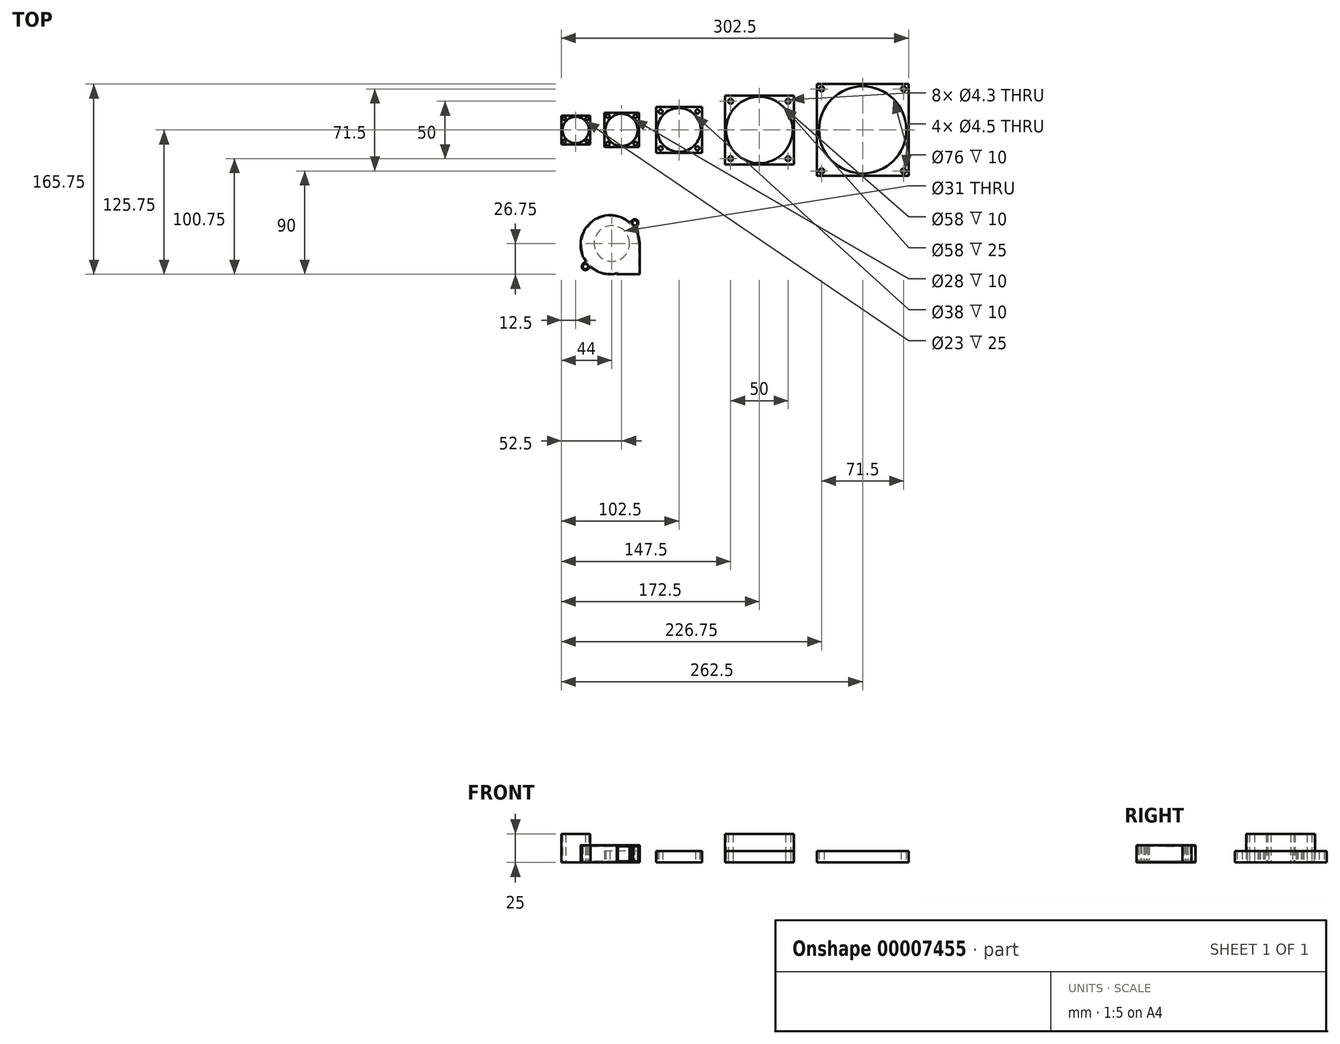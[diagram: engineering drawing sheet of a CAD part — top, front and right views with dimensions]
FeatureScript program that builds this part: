
annotation { "Feature Type Name" : "Feature", "Feature Type Description" : "" }
export const myFeature = defineFeature(function(context is Context, id is Id, definition is map)
    precondition{}
    {
        {
            var Q0;
            Q0=qCreatedBy(makeId("Top.planeOp"),FACE);
            var sketch = newSketch(context, id + "F0", { "sketchPlane" : qUnion([Q0])});
            skLineSegment(sketch, "E0", {"start": v(0, 0) * mm, "end": v(333.95, 0) * mm, "construction": true});
            skLineSegment(sketch, "E1.rect.bottom", {"start": v(32.5, 12.5) * mm, "end": v(7.5, 12.5) * mm});
            skLineSegment(sketch, "E1.rect.top", {"start": v(32.5, -12.5) * mm, "end": v(7.5, -12.5) * mm});
            skLineSegment(sketch, "E1.rect.left", {"start": v(32.5, 12.5) * mm, "end": v(32.5, -12.5) * mm});
            skLineSegment(sketch, "E1.rect.right", {"start": v(7.5, 12.5) * mm, "end": v(7.5, -12.5) * mm});
            skPoint(sketch, "E1.rect.middle", {"position": v(20, 0) * mm});
            skLineSegment(sketch, "E2.rect.bottom", {"start": v(30, 10) * mm, "end": v(10, 10) * mm, "construction": true});
            skLineSegment(sketch, "E2.rect.top", {"start": v(30, -10) * mm, "end": v(10, -10) * mm, "construction": true});
            skLineSegment(sketch, "E2.rect.left", {"start": v(30, 10) * mm, "end": v(30, -10) * mm, "construction": true});
            skLineSegment(sketch, "E2.rect.right", {"start": v(10, 10) * mm, "end": v(10, -10) * mm, "construction": true});
            skLineSegment(sketch, "E3.rect.bottom", {"start": v(72, 12) * mm, "end": v(48, 12) * mm, "construction": true});
            skLineSegment(sketch, "E3.rect.top", {"start": v(72, -12) * mm, "end": v(48, -12) * mm, "construction": true});
            skLineSegment(sketch, "E3.rect.left", {"start": v(72, 12) * mm, "end": v(72, -12) * mm, "construction": true});
            skLineSegment(sketch, "E3.rect.right", {"start": v(48, 12) * mm, "end": v(48, -12) * mm, "construction": true});
            skPoint(sketch, "E3.rect.middle", {"position": v(60, 0) * mm});
            skLineSegment(sketch, "E4.rect.bottom", {"start": v(126, 16) * mm, "end": v(94, 16) * mm, "construction": true});
            skLineSegment(sketch, "E4.rect.top", {"start": v(126, -16) * mm, "end": v(94, -16) * mm, "construction": true});
            skLineSegment(sketch, "E4.rect.left", {"start": v(126, 16) * mm, "end": v(126, -16) * mm, "construction": true});
            skLineSegment(sketch, "E4.rect.right", {"start": v(94, 16) * mm, "end": v(94, -16) * mm, "construction": true});
            skPoint(sketch, "E4.rect.middle", {"position": v(110, 0) * mm});
            skLineSegment(sketch, "E5.rect.bottom", {"start": v(305.75, 35.75) * mm, "end": v(234.25, 35.75) * mm, "construction": true});
            skLineSegment(sketch, "E5.rect.top", {"start": v(305.75, -35.75) * mm, "end": v(234.25, -35.75) * mm, "construction": true});
            skLineSegment(sketch, "E5.rect.left", {"start": v(305.75, 35.75) * mm, "end": v(305.75, -35.75) * mm, "construction": true});
            skLineSegment(sketch, "E5.rect.right", {"start": v(234.25, 35.75) * mm, "end": v(234.25, -35.75) * mm, "construction": true});
            skPoint(sketch, "E5.rect.middle", {"position": v(270, 0) * mm});
            skLineSegment(sketch, "E6.rect.bottom", {"start": v(75, 15) * mm, "end": v(45, 15) * mm});
            skLineSegment(sketch, "E6.rect.top", {"start": v(75, -15) * mm, "end": v(45, -15) * mm});
            skLineSegment(sketch, "E6.rect.left", {"start": v(75, 15) * mm, "end": v(75, -15) * mm});
            skLineSegment(sketch, "E6.rect.right", {"start": v(45, 15) * mm, "end": v(45, -15) * mm});
            skLineSegment(sketch, "E7.rect.bottom", {"start": v(90, 20) * mm, "end": v(130, 20) * mm});
            skLineSegment(sketch, "E7.rect.top", {"start": v(90, -20) * mm, "end": v(130, -20) * mm});
            skLineSegment(sketch, "E7.rect.left", {"start": v(90, 20) * mm, "end": v(90, -20) * mm});
            skLineSegment(sketch, "E7.rect.right", {"start": v(130, 20) * mm, "end": v(130, -20) * mm});
            skLineSegment(sketch, "E8.rect.bottom", {"start": v(230, 40) * mm, "end": v(310, 40) * mm});
            skLineSegment(sketch, "E8.rect.top", {"start": v(230, -40) * mm, "end": v(310, -40) * mm});
            skLineSegment(sketch, "E8.rect.left", {"start": v(230, 40) * mm, "end": v(230, -40) * mm});
            skLineSegment(sketch, "E8.rect.right", {"start": v(310, 40) * mm, "end": v(310, -40) * mm});
            skCircle(sketch, "E9", {"center": v(20, 0) * mm, "radius": 11.5 * mm});
            skCircle(sketch, "E10", {"center": v(10, 10) * mm, "radius": 1.4 * mm});
            skCircle(sketch, "E11", {"center": v(30, 10) * mm, "radius": 1.4 * mm});
            skCircle(sketch, "E12", {"center": v(30, -10) * mm, "radius": 1.4 * mm});
            skCircle(sketch, "E13", {"center": v(10, -10) * mm, "radius": 1.4 * mm});
            skCircle(sketch, "E14", {"center": v(48, 12) * mm, "radius": 1.6 * mm});
            skCircle(sketch, "E15", {"center": v(72, 12) * mm, "radius": 1.6 * mm});
            skCircle(sketch, "E16", {"center": v(72, -12) * mm, "radius": 1.6 * mm});
            skCircle(sketch, "E17", {"center": v(48, -12) * mm, "radius": 1.6 * mm});
            skCircle(sketch, "E18", {"center": v(60, 0) * mm, "radius": 14 * mm});
            skCircle(sketch, "E19", {"center": v(94, 16) * mm, "radius": 1.75 * mm});
            skCircle(sketch, "E20", {"center": v(126, 16) * mm, "radius": 1.75 * mm});
            skCircle(sketch, "E21", {"center": v(126, -16) * mm, "radius": 1.75 * mm});
            skCircle(sketch, "E22", {"center": v(94, -16) * mm, "radius": 1.75 * mm});
            skCircle(sketch, "E23", {"center": v(110, 0) * mm, "radius": 19 * mm});
            skLineSegment(sketch, "E24.rect.bottom", {"start": v(210, 30) * mm, "end": v(150, 30) * mm});
            skLineSegment(sketch, "E24.rect.top", {"start": v(210, -30) * mm, "end": v(150, -30) * mm});
            skLineSegment(sketch, "E24.rect.left", {"start": v(210, 30) * mm, "end": v(210, -30) * mm});
            skLineSegment(sketch, "E24.rect.right", {"start": v(150, 30) * mm, "end": v(150, -30) * mm});
            skPoint(sketch, "E24.rect.middle", {"position": v(180, 0) * mm});
            skLineSegment(sketch, "E25.rect.bottom", {"start": v(205, 25) * mm, "end": v(155, 25) * mm, "construction": true});
            skLineSegment(sketch, "E25.rect.top", {"start": v(205, -25) * mm, "end": v(155, -25) * mm, "construction": true});
            skLineSegment(sketch, "E25.rect.left", {"start": v(205, 25) * mm, "end": v(205, -25) * mm, "construction": true});
            skLineSegment(sketch, "E25.rect.right", {"start": v(155, 25) * mm, "end": v(155, -25) * mm, "construction": true});
            skCircle(sketch, "E26", {"center": v(155, 25) * mm, "radius": 2.15 * mm});
            skCircle(sketch, "E27", {"center": v(205, 25) * mm, "radius": 2.15 * mm});
            skCircle(sketch, "E28", {"center": v(205, -25) * mm, "radius": 2.15 * mm});
            skCircle(sketch, "E29", {"center": v(155, -25) * mm, "radius": 2.15 * mm});
            skCircle(sketch, "E30", {"center": v(180, 0) * mm, "radius": 29 * mm});
            skCircle(sketch, "E31", {"center": v(234.25, 35.75) * mm, "radius": 2.25 * mm});
            skCircle(sketch, "E32", {"center": v(305.75, 35.75) * mm, "radius": 2.25 * mm});
            skCircle(sketch, "E33", {"center": v(305.75, -35.75) * mm, "radius": 2.25 * mm});
            skCircle(sketch, "E34", {"center": v(234.25, -35.75) * mm, "radius": 2.25 * mm});
            skCircle(sketch, "E35", {"center": v(270, 0) * mm, "radius": 38 * mm});
            skPoint(sketch, "E36", {"position": v(50, -100) * mm});
            skPoint(sketch, "E37", {"position": v(28.5, -119) * mm});
            skPoint(sketch, "E38", {"position": v(71.5, -81) * mm});
            skCircle(sketch, "E39", {"center": v(71.5, -81) * mm, "radius": 2.2 * mm});
            skCircle(sketch, "E40", {"center": v(28.5, -119) * mm, "radius": 2.2 * mm});
            skArc(sketch, "E41", {"start": v(73.62, -83.4) * mm, "mid": v(73.9, -78.88) * mm, "end": v(69.38, -78.6) * mm});
            skArc(sketch, "E42", {"start": v(26.38, -116.6) * mm, "mid": v(26.1, -121.12) * mm, "end": v(30.62, -121.4) * mm});
            skLineSegment(sketch, "E43", {"start": v(50, -100) * mm, "end": v(24.25, -100) * mm, "construction": true});
            skLineSegment(sketch, "E44", {"start": v(50, -100) * mm, "end": v(50, -125.75) * mm, "construction": true});
            skLineSegment(sketch, "E45", {"start": v(50, -100) * mm, "end": v(75.75, -100) * mm, "construction": true});
            skLineSegment(sketch, "E46", {"start": v(28.5, -119) * mm, "end": v(71.5, -81) * mm, "construction": true});
            skLineSegment(sketch, "E47", {"start": v(75.75, -100) * mm, "end": v(75.75, -125.75) * mm});
            skLineSegment(sketch, "E48", {"start": v(75.75, -125.75) * mm, "end": v(55.75, -125.75) * mm});
            skLineSegment(sketch, "E49", {"start": v(55.75, -125.75) * mm, "end": v(55.75, -125.1) * mm});
            skLineSegment(sketch, "E50", {"start": v(73.62, -83.4) * mm, "end": v(30.62, -121.4) * mm});
            skLineSegment(sketch, "E51", {"start": v(26.38, -116.6) * mm, "end": v(69.38, -78.6) * mm});
            skArc(sketch, "E52.trimOffspring", {"start": v(32.97, -119.32) * mm, "mid": v(67.05, -119.3) * mm, "end": v(71.26, -85.48) * mm});
            skArc(sketch, "E53.trimOffspring", {"start": v(67.03, -80.68) * mm, "mid": v(32.95, -80.7) * mm, "end": v(28.74, -114.52) * mm});
            skCircle(sketch, "E54", {"center": v(51.5, -99) * mm, "radius": 15.5 * mm});
            skSolve(sketch);
        }
        {
            var Q0;
            Q0=makeQuery(id+"F0.imprint","IMPRINT",FACE,{"disambiguationData":[TD([[makeQuery(id+"F0.imprint","IMPRINT",EDGE,{"derivedFrom":sQuery(id+"F0.wireOp",EDGE,"E1.rect.bottom")}),1.0]])]});
            extrude(context, id + "F1", {"entities" : qUnion([Q0]), "depth" : 25 * mm});
        }
        {
            var Q0;
            Q0=makeQuery(id+"F0.imprint","IMPRINT",FACE,{"disambiguationData":[TD([[makeQuery(id+"F0.imprint","IMPRINT",EDGE,{"derivedFrom":sQuery(id+"F0.wireOp",EDGE,"E6.rect.bottom")}),1.0]])]});
            extrude(context, id + "F2", {"entities" : qUnion([Q0]), "depth" : 10 * mm});
        }
        {
            var Q0;
            Q0=makeQuery(id+"F0.imprint","IMPRINT",FACE,{"disambiguationData":[TD([[makeQuery(id+"F0.imprint","IMPRINT",EDGE,{"derivedFrom":sQuery(id+"F0.wireOp",EDGE,"E7.rect.bottom")}),-1.0]])]});
            extrude(context, id + "F3", {"entities" : qUnion([Q0]), "depth" : 10 * mm});
        }
        {
            var Q0;
            Q0=makeQuery(id+"F0.imprint","IMPRINT",FACE,{"disambiguationData":[TD([[makeQuery(id+"F0.imprint","IMPRINT",EDGE,{"derivedFrom":sQuery(id+"F0.wireOp",EDGE,"E24.rect.bottom")}),1.0]])]});
            extrude(context, id + "F4", {"entities" : qUnion([Q0]), "depth" : 10 * mm});
        }
        {
            var Q0;
            Q0=makeQuery(id+"F0.imprint","IMPRINT",FACE,{"disambiguationData":[TD([[makeQuery(id+"F0.imprint","IMPRINT",EDGE,{"derivedFrom":sQuery(id+"F0.wireOp",EDGE,"E24.rect.bottom")}),1.0]])]});
            extrude(context, id + "F5", {"entities" : qUnion([Q0]), "depth" : 25 * mm});
        }
        {
            var Q0;
            Q0=makeQuery(id+"F0.imprint","IMPRINT",FACE,{"disambiguationData":[TD([[makeQuery(id+"F0.imprint","IMPRINT",EDGE,{"derivedFrom":sQuery(id+"F0.wireOp",EDGE,"E8.rect.bottom")}),-1.0]])]});
            extrude(context, id + "F6", {"entities" : qUnion([Q0]), "depth" : 10 * mm});
        }
        {
            var Q0;
            {var subQ2=sQuery(id+"F0.wireOp",EDGE,"E47");Q0=makeQuery(id+"F0.imprint","IMPRINT",FACE,{"disambiguationData":[TD([[makeQuery(id+"F0.imprint","IMPRINT",EDGE,{"derivedFrom":subQ2}),-1.0]])]});}
            var Q1;
            {var subQ1=sQuery(id+"F0.wireOp",EDGE,"E50");var subQ4=sQuery(id+"F0.wireOp",EDGE,"E52.trimOffspring");var subQ5=makeQuery(id+"F0.imprint","INTERSECT",VERTEX,{"disambiguationData":[OD(1.0)],"derivedFrom":[subQ1,subQ4]});Q1=makeQuery(id+"F0.imprint","IMPRINT",FACE,{"disambiguationData":[TD([[makeQuery(id+"F0.imprint","IMPRINT",EDGE,{"disambiguationData":[TD([[subQ5,-1.0]])],"derivedFrom":subQ1}),1.0]])]});}
            var Q2;
            Q2=makeQuery(id+"F0.imprint","IMPRINT",FACE,{"disambiguationData":[TD([[makeQuery(id+"F0.imprint","IMPRINT",EDGE,{"derivedFrom":sQuery(id+"F0.wireOp",EDGE,"E39")}),-1.0]])]});
            var Q3;
            {var subQ4=sQuery(id+"F0.wireOp",EDGE,"E53.trimOffspring");Q3=makeQuery(id+"F0.imprint","IMPRINT",FACE,{"disambiguationData":[TD([[makeQuery(id+"F0.imprint","IMPRINT",EDGE,{"derivedFrom":subQ4}),1.0]])]});}
            var Q4;
            Q4=makeQuery(id+"F0.imprint","IMPRINT",FACE,{"disambiguationData":[TD([[makeQuery(id+"F0.imprint","IMPRINT",EDGE,{"derivedFrom":sQuery(id+"F0.wireOp",EDGE,"E40")}),-1.0]])]});
            var Q5;
            {var subQ0=sQuery(id+"F0.wireOp",EDGE,"E54");var subQ1=sQuery(id+"F0.wireOp",EDGE,"E51");var subQ3=makeQuery(id+"F0.imprint","INTERSECT",VERTEX,{"disambiguationData":[OD(0.0)],"derivedFrom":[subQ1,subQ0]});Q5=makeQuery(id+"F0.imprint","IMPRINT",FACE,{"disambiguationData":[TD([[makeQuery(id+"F0.imprint","IMPRINT",EDGE,{"disambiguationData":[TD([[subQ3,-1.0]])],"derivedFrom":subQ1}),1.0]])]});}
            var Q6;
            {var subQ0=sQuery(id+"F0.wireOp",EDGE,"E54");var subQ3=sQuery(id+"F0.wireOp",EDGE,"E50");var subQ6=makeQuery(id+"F0.imprint","INTERSECT",VERTEX,{"disambiguationData":[OD(0.0)],"derivedFrom":[subQ3,subQ0]});Q6=makeQuery(id+"F0.imprint","IMPRINT",FACE,{"disambiguationData":[TD([[makeQuery(id+"F0.imprint","IMPRINT",EDGE,{"disambiguationData":[TD([[subQ6,-1.0]])],"derivedFrom":subQ3}),-1.0]])]});}
            var Q7;
            {var subQ0=sQuery(id+"F0.wireOp",EDGE,"E54");var subQ1=sQuery(id+"F0.wireOp",EDGE,"E50");var subQ3=makeQuery(id+"F0.imprint","INTERSECT",VERTEX,{"disambiguationData":[OD(0.0)],"derivedFrom":[subQ1,subQ0]});Q7=makeQuery(id+"F0.imprint","IMPRINT",FACE,{"disambiguationData":[TD([[makeQuery(id+"F0.imprint","IMPRINT",EDGE,{"disambiguationData":[TD([[subQ3,-1.0]])],"derivedFrom":subQ1}),1.0]])]});}
            extrude(context, id + "F7", {"entities" : qUnion([Q0, Q1, Q2, Q3, Q4, Q5, Q6, Q7]), "depth" : 15 * mm});
        }
        {
            var Q0;
            {var subQ0=sQuery(id+"F0.wireOp",EDGE,"E54");var subQ1=sQuery(id+"F0.wireOp",EDGE,"E51");var subQ3=makeQuery(id+"F0.imprint","INTERSECT",VERTEX,{"disambiguationData":[OD(0.0)],"derivedFrom":[subQ1,subQ0]});Q0=makeQuery(id+"F0.imprint","IMPRINT",FACE,{"disambiguationData":[TD([[makeQuery(id+"F0.imprint","IMPRINT",EDGE,{"disambiguationData":[TD([[subQ3,-1.0]])],"derivedFrom":subQ1}),1.0]])]});}
            var Q1;
            {var subQ0=sQuery(id+"F0.wireOp",EDGE,"E54");var subQ3=sQuery(id+"F0.wireOp",EDGE,"E50");var subQ6=makeQuery(id+"F0.imprint","INTERSECT",VERTEX,{"disambiguationData":[OD(0.0)],"derivedFrom":[subQ3,subQ0]});Q1=makeQuery(id+"F0.imprint","IMPRINT",FACE,{"disambiguationData":[TD([[makeQuery(id+"F0.imprint","IMPRINT",EDGE,{"disambiguationData":[TD([[subQ6,-1.0]])],"derivedFrom":subQ3}),-1.0]])]});}
            var Q2;
            {var subQ0=sQuery(id+"F0.wireOp",EDGE,"E54");var subQ1=sQuery(id+"F0.wireOp",EDGE,"E50");var subQ3=makeQuery(id+"F0.imprint","INTERSECT",VERTEX,{"disambiguationData":[OD(0.0)],"derivedFrom":[subQ1,subQ0]});Q2=makeQuery(id+"F0.imprint","IMPRINT",FACE,{"disambiguationData":[TD([[makeQuery(id+"F0.imprint","IMPRINT",EDGE,{"disambiguationData":[TD([[subQ3,-1.0]])],"derivedFrom":subQ1}),1.0]])]});}
            extrude(context, id + "F8", {"entities" : qUnion([Q0, Q1, Q2]), "operationType" : NewBodyOperationType.REMOVE, "depth" : 10 * mm});
        }
        {
            var Q0;
            Q0=makeQuery(id+"F7.opExtrude","SWEPT_FACE",FACE,{"disambiguationData":[OSD([sQuery(id+"F0.wireOp",EDGE,"E48")])]});
            var Q1;
            Q1=makeQuery(id+"F8.boolean.opBoolean","COPY",FACE,{"derivedFrom":makeQuery(id+"F8.opExtrude","CAP_FACE",FACE,{"disambiguationData":[OSD([sQuery(id+"F0.wireOp",EDGE,"E54")])],"isStart":false})});
            var Q2;
            Q2=makeQuery(id+"F8.boolean.opBoolean","COPY",FACE,{"derivedFrom":makeQuery(id+"F8.opExtrude","SWEPT_FACE",FACE,{"disambiguationData":[OSD([sQuery(id+"F0.wireOp",EDGE,"E54")])]})});
            shell(context, id + "F9", {"entities" : qUnion([Q0, Q1, Q2]), "thickness" : 1 * mm});
        }
    });
